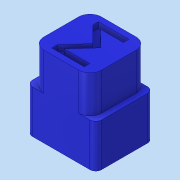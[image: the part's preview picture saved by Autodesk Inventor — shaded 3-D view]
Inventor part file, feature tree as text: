
AUTODESK INVENTOR PART (.ipt)
format: ipt  version: 2018 (Build 220112000, 112)  size: 167,936 bytes
history: native  units: mm
features: sketch x3, extrude x2, fillet x2, other x1, projected_geometry x1
ambient origin geometry x8: Origin, YZ Plane, XZ Plane, XY Plane, X Axis, Y Axis, Z Axis, Center Point
bodies: Volumenkörper1 (feature_tree)
feature tree (9):
  extrude  "Extrusion1"  Depth=10.0mm
  extrude  "Extrusion2"  Depth=10.0mm
  fillet  "Rundung1"  Radius=10.0mm
  fillet  "Rundung2"  Radius=6.5mm
  other  "Prägen1"
  sketch  "Skizze1"  dims[d0=12.0mm d1=10.0mm]
  sketch  "Skizze2"  dims[d2=14.0mm d3=0.0mm d4=10.0mm d5=10.0mm d6=6.5mm d7=0.0mm]
  sketch  "Skizze3"  dims[d8=2.0mm d9=1.0mm d10=1.0mm d11=1.0mm d12=1.0mm d13=3.490659mm]
  projected_geometry  "Projizierte Kontur1"
